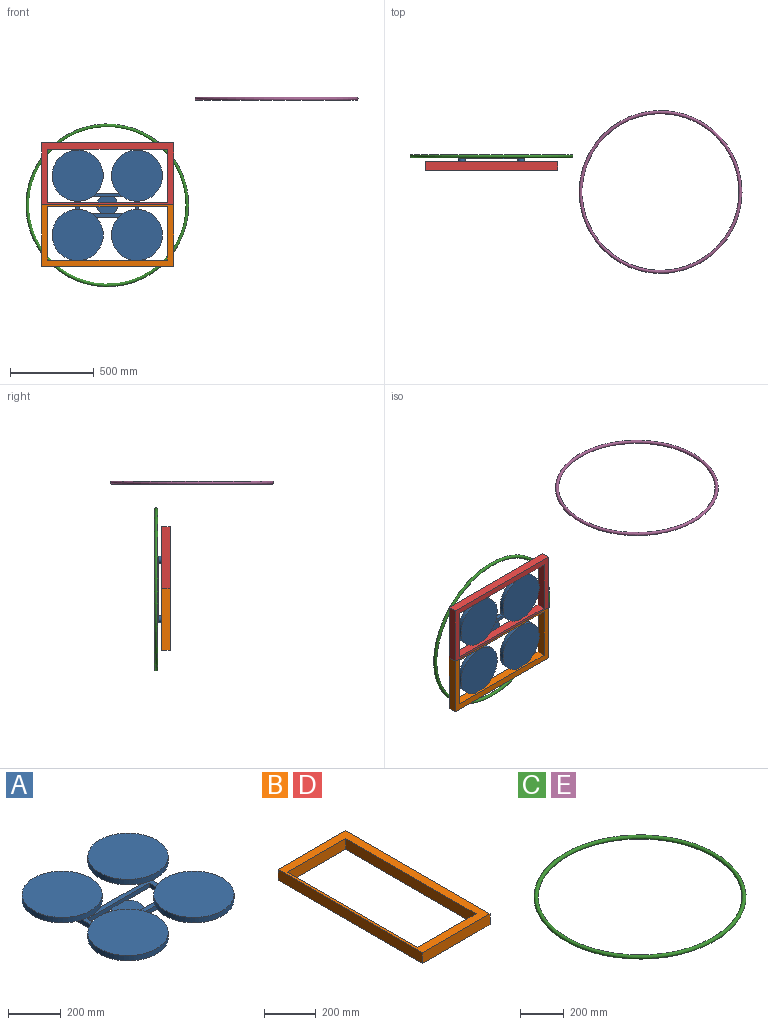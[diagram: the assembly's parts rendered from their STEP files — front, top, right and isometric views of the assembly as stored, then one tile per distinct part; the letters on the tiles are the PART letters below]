
ASSEMBLY  parts=5 mates=4
PART A: 49 faces, bbox 658.4x658.4x75.9 mm
  f0: plane 333.55x20mm, normal (0,-1,0), area 6296.1mm2, adj f2,f14,f15,f17,f46,f47,f48
  f1: plane 333.55x20mm, normal (0,1,0), area 6296.1mm2, adj f2,f14,f15,f17,f46,f47,f48
  f2: plane 373.55x316.62mm, normal (0,0,1), area 25870.1mm2, adj f0,f1,f3,f4,f6,f8,f9,f10
  f3: plane 333.55x20mm, normal (0,1,0), area 6671.1mm2, adj f2,f4,f16,f17
  f4: plane 106.78x20mm, normal (1,0,0), area 2135.5mm2, adj f2,f3,f5,f17,f23
  f5: plane 20x20mm, normal (0,1,0), area 400mm2, adj f4,f6,f17,f23
  f6: plane 353.55x20mm, normal (-1,0,0), area 7071.1mm2, adj f2,f5,f7,f17,f18,f23
  f7: plane 20x20mm, normal (0,-1,0), area 400mm2, adj f6,f8,f17,f18
  f8: plane 106.78x20mm, normal (1,0,0), area 2135.5mm2, adj f2,f7,f9,f17,f18
  f9: plane 333.55x20mm, normal (0,-1,0), area 6671.1mm2, adj f2,f8,f10,f17
  f10: plane 106.78x20mm, normal (-1,0,0), area 2135.5mm2, adj f2,f9,f11,f17,f27
  f11: plane 20x20mm, normal (0,-1,0), area 400mm2, adj f10,f12,f17,f27
  f12: plane 353.55x20mm, normal (1,0,0), area 7071.1mm2, adj f2,f11,f13,f17,f26,f27
  f13: plane 20x20mm, normal (0,1,0), area 400mm2, adj f12,f16,f17,f26
  f14: plane 100x20mm, normal (1,0,0), area 2000mm2, adj f0,f1,f2,f17
  f15: plane 100x20mm, normal (-1,0,0), area 2000mm2, adj f0,f1,f2,f17
  f16: plane 106.78x20mm, normal (-1,0,0), area 2135.5mm2, adj f2,f3,f13,f17,f26
  f17: plane 373.55x353.55mm, normal (0,0,-1), area 38478.8mm2, adj f0,f1,f3,f4,f5,f6,f7,f8
  f18: plane 42x39.47mm, normal (0,0,-1), area 981.9mm2, adj f6,f7,f8,f19
  f19: cylinder r=21mm len=42mm, axis (0,0,-1), area 3289.4mm2, adj f2,f18,f20
  f20: plane 42x42mm, normal (0,0,1), area 1086.8mm2, adj f19,f30
  f21: cylinder r=21mm len=42mm, axis (0,0,-1), area 3289.4mm2, adj f2,f22,f23
  f22: plane 42x42mm, normal (0,0,1), area 1086.8mm2, adj f21,f31
  f23: plane 42x39.47mm, normal (0,0,-1), area 981.9mm2, adj f4,f5,f6,f21
  f24: cylinder r=21mm len=42mm, axis (0,0,-1), area 3289.4mm2, adj f2,f25,f26
  f25: plane 42x42mm, normal (0,0,1), area 1086.8mm2, adj f24,f32
  f26: plane 42x39.47mm, normal (0,0,-1), area 981.9mm2, adj f12,f13,f16,f24
  f27: plane 42x39.47mm, normal (0,0,-1), area 981.9mm2, adj f10,f11,f12,f28
  f28: cylinder r=21mm len=42mm, axis (0,0,-1), area 3289.4mm2, adj f2,f27,f29
  f29: plane 42x42mm, normal (0,0,1), area 1086.8mm2, adj f28,f33
  f30: cylinder r=9.75mm len=19.5mm, axis (0,0,-1), area 367.6mm2, adj f20,f36
  f31: cylinder r=9.75mm len=19.5mm, axis (0,0,-1), area 367.6mm2, adj f22,f39
  f32: cylinder r=9.75mm len=19.5mm, axis (0,0,-1), area 367.6mm2, adj f25,f42
  f33: cylinder r=9.75mm len=19.5mm, axis (0,0,-1), area 367.6mm2, adj f29,f45
  f34: cylinder r=152.4mm len=304.8mm, axis (0,0,-1), area 23938.9mm2, adj f35,f36
  f35: plane 304.8x304.8mm, normal (0,0,1), area 72965.9mm2, adj f34
  f36: plane 304.8x304.8mm, normal (0,0,-1), area 72667.2mm2, adj f30,f34
  f37: cylinder r=152.4mm len=304.8mm, axis (0,0,-1), area 23938.9mm2, adj f38,f39
  f38: plane 304.8x304.8mm, normal (0,0,1), area 72965.9mm2, adj f37
  f39: plane 304.8x304.8mm, normal (0,0,-1), area 72667.2mm2, adj f31,f37
  f40: cylinder r=152.4mm len=304.8mm, axis (0,0,-1), area 23938.9mm2, adj f41,f42
  f41: plane 304.8x304.8mm, normal (0,0,1), area 72965.9mm2, adj f40
  f42: plane 304.8x304.8mm, normal (0,0,-1), area 72667.2mm2, adj f32,f40
  f43: cylinder r=152.4mm len=304.8mm, axis (0,0,-1), area 23938.9mm2, adj f44,f45
  f44: plane 304.8x304.8mm, normal (0,0,1), area 72965.9mm2, adj f43
  f45: plane 304.8x304.8mm, normal (0,0,-1), area 72667.2mm2, adj f33,f43
  f46: plane 125x100mm, normal (0,0,1), area 10994.5mm2, adj f0,f1,f47,f48
  f47: cylinder r=62.5mm len=100mm, axis (0,0,-1), area 579.6mm2, adj f0,f1,f17,f46
  f48: cylinder r=62.5mm len=100mm, axis (0,0,-1), area 579.6mm2, adj f0,f1,f17,f46
PART B: 10 faces, bbox 368.3x787.4x50.8 mm
  f0: plane 317.5x50.8mm, normal (0,-1,0), area 16129mm2, adj f1,f7,f8,f9
  f1: plane 711.2x50.8mm, normal (-1,0,0), area 36129mm2, adj f0,f2,f8,f9
  f2: plane 317.5x50.8mm, normal (0,1,0), area 16129mm2, adj f1,f7,f8,f9
  f3: plane 368.3x50.8mm, normal (0,1,0), area 18709.6mm2, adj f4,f6,f8,f9
  f4: plane 787.4x50.8mm, normal (-1,0,0), area 39999.9mm2, adj f3,f5,f8,f9
  f5: plane 368.3x50.8mm, normal (0,-1,0), area 18709.6mm2, adj f4,f6,f8,f9
  f6: plane 787.4x50.8mm, normal (1,0,0), area 39999.9mm2, adj f3,f5,f8,f9
  f7: plane 711.2x50.8mm, normal (1,0,0), area 36129mm2, adj f0,f2,f8,f9
  f8: plane 787.4x368.3mm, normal (0,0,1), area 64193.4mm2, adj f0,f1,f2,f3,f4,f5,f6,f7
  f9: plane 787.4x368.3mm, normal (0,0,-1), area 64193.4mm2, adj f0,f1,f2,f3,f4,f5,f6,f7
PART C: 1 faces, bbox 1051.6x1051.6x19.1 mm
  f0: torus R=476.25mm, axis (0,0,1), area 179085.2mm2
PART D: same geometry as B
PART E: same geometry as C
PLACE A rot(axis=(1,0,0),90deg) t=(0,5,0)mm
PLACE B rot(axis=(-0.58,0.58,0.58),120deg) t=(1.3,-83.92,-167.22)mm
PLACE C rot(axis=(1,0,0),90deg) t=(0,0,0)mm
PLACE D rot(axis=(0.58,-0.58,0.58),120deg) t=(1.3,-33.12,175.68)mm
PLACE E t=(1009.37,-214.19,635.23)mm
MATE planar D.f3 <-> B.f3  axis (-1,0,0) through (-392.4,-58.52,188.38)mm
MATE planar D.f4 <-> B.f4  axis (0,0,-1) through (1.3,-58.52,4.23)mm
MATE fastened C.f0 <-> A.f47  axis (0,-1,0) through (0,0,0)mm
MATE planar B.f9 <-> D.f8  axis (0,-1,0) through (1.3,-83.92,-224.6)mm
